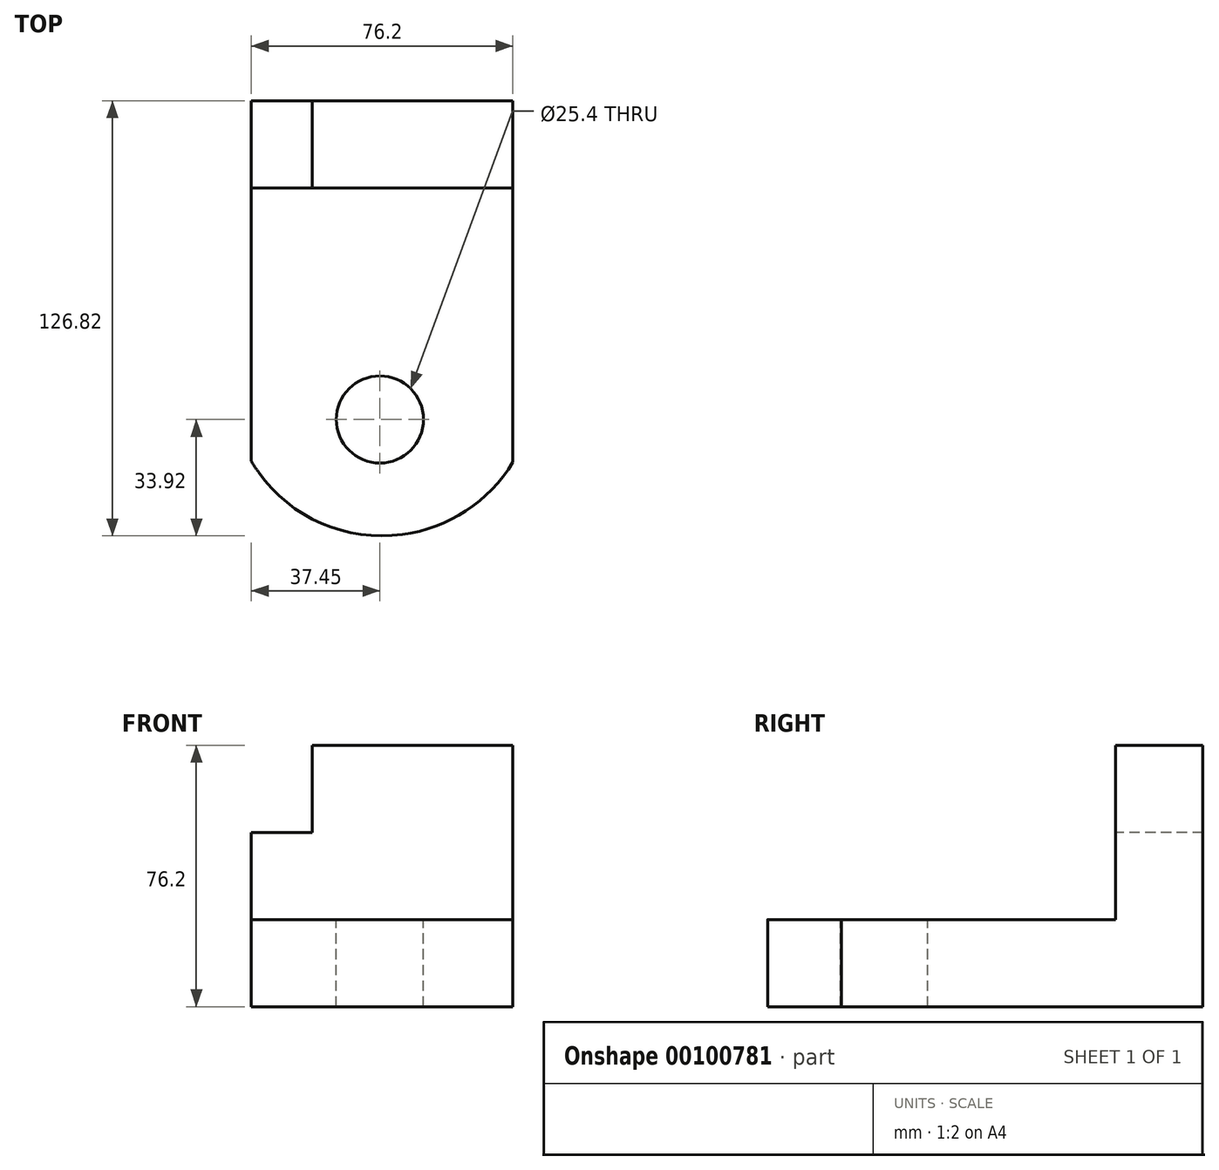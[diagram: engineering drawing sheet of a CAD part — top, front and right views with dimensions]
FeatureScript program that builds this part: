
annotation { "Feature Type Name" : "Feature", "Feature Type Description" : "" }
export const myFeature = defineFeature(function(context is Context, id is Id, definition is map)
    precondition{}
    {
        {
            var Q0;
            Q0=qCreatedBy(makeId("Top.planeOp"),FACE);
            var sketch = newSketch(context, id + "F0", { "sketchPlane" : qUnion([Q0])});
            skLineSegment(sketch, "E0.bottom", {"start": v(-37.45, 64) * mm, "end": v(38.75, 64) * mm});
            skLineSegment(sketch, "E0.top", {"start": v(-37.45, -63) * mm, "end": v(38.75, -63) * mm});
            skLineSegment(sketch, "E0.left", {"start": v(-37.45, 64) * mm, "end": v(-37.45, -63) * mm});
            skLineSegment(sketch, "E0.right", {"start": v(38.75, 64) * mm, "end": v(38.75, -63) * mm});
            skSolve(sketch);
        }
        {
            var Q0;
            Q0=makeQuery(id+"F0.imprint","IMPRINT",FACE,{"disambiguationData":[TD([[makeQuery(id+"F0.imprint","IMPRINT",EDGE,{"derivedFrom":sQuery(id+"F0.wireOp",EDGE,"E0.bottom")}),-1.0]])]});
            extrude(context, id + "F1", {"entities" : qUnion([Q0]), "depth" : 25.4 * mm});
        }
        {
            var Q0;
            Q0=makeQuery(id+"F1.opExtrude","CAP_FACE",FACE,{"disambiguationData":[OSD([sQuery(id+"F0.wireOp",EDGE,"E0.bottom"),sQuery(id+"F0.wireOp",EDGE,"E0.top"),sQuery(id+"F0.wireOp",EDGE,"E0.left"),sQuery(id+"F0.wireOp",EDGE,"E0.right")])],"isStart":false});
            var sketch = newSketch(context, id + "F2", { "sketchPlane" : qUnion([Q0])});
            skLineSegment(sketch, "E1.bottom", {"start": v(-37.45, 64) * mm, "end": v(38.75, 64) * mm});
            skLineSegment(sketch, "E1.top", {"start": v(-37.45, 38.6) * mm, "end": v(38.75, 38.6) * mm});
            skLineSegment(sketch, "E1.left", {"start": v(-37.45, 64) * mm, "end": v(-37.45, 38.6) * mm});
            skLineSegment(sketch, "E1.right", {"start": v(38.75, 64) * mm, "end": v(38.75, 38.6) * mm});
            skArc(sketch, "E2", {"start": v(-37.45, -47.3) * mm, "mid": v(0.6, -62.48) * mm, "end": v(38.75, -47.59) * mm});
            skSolve(sketch);
        }
        {
            var Q0;
            Q0=makeQuery(id+"F2.imprint","IMPRINT",FACE,{"disambiguationData":[TD([[makeQuery(id+"F2.imprint","IMPRINT",EDGE,{"derivedFrom":sQuery(id+"F2.wireOp",EDGE,"E1.bottom")}),-1.0]])]});
            extrude(context, id + "F3", {"entities" : qUnion([Q0]), "operationType" : NewBodyOperationType.ADD, "depth" : 25.4 * mm});
        }
        {
            var Q0;
            Q0=makeQuery(id+"F3.opExtrude","CAP_FACE",FACE,{"disambiguationData":[OSD([sQuery(id+"F2.wireOp",EDGE,"E1.bottom"),sQuery(id+"F2.wireOp",EDGE,"E1.top"),sQuery(id+"F2.wireOp",EDGE,"E1.left"),sQuery(id+"F2.wireOp",EDGE,"E1.right")])],"isStart":false});
            var sketch = newSketch(context, id + "F4", { "sketchPlane" : qUnion([Q0])});
            skLineSegment(sketch, "E3.bottom", {"start": v(-19.67, 64) * mm, "end": v(38.75, 64) * mm});
            skLineSegment(sketch, "E3.top", {"start": v(-19.67, 38.6) * mm, "end": v(38.75, 38.6) * mm});
            skLineSegment(sketch, "E3.left", {"start": v(-19.67, 64) * mm, "end": v(-19.67, 38.6) * mm});
            skLineSegment(sketch, "E3.right", {"start": v(38.75, 64) * mm, "end": v(38.75, 38.6) * mm});
            skSolve(sketch);
        }
        {
            var Q0;
            Q0=makeQuery(id+"F4.imprint","IMPRINT",FACE,{"disambiguationData":[TD([[makeQuery(id+"F4.imprint","IMPRINT",EDGE,{"derivedFrom":sQuery(id+"F4.wireOp",EDGE,"E3.bottom")}),-1.0]])]});
            extrude(context, id + "F5", {"entities" : qUnion([Q0]), "operationType" : NewBodyOperationType.ADD, "depth" : 25.4 * mm});
        }
        {
            var Q0;
            Q0=makeQuery(id+"F1.opExtrude","CAP_FACE",FACE,{"disambiguationData":[OSD([sQuery(id+"F0.wireOp",EDGE,"E0.bottom"),sQuery(id+"F0.wireOp",EDGE,"E0.top"),sQuery(id+"F0.wireOp",EDGE,"E0.left"),sQuery(id+"F0.wireOp",EDGE,"E0.right")])],"isStart":false});
            var sketch = newSketch(context, id + "F6", { "sketchPlane" : qUnion([Q0])});
            skArc(sketch, "E4", {"start": v(-37.45, -41.05) * mm, "mid": v(0.57, -62.77) * mm, "end": v(38.75, -41.34) * mm});
            skSolve(sketch);
        }
        {
            var Q0;
            Q0=makeQuery(id+"F6.imprint","IMPRINT",FACE,{"disambiguationData":[TD([[makeQuery(id+"F6.imprint","IMPRINT",EDGE,{"derivedFrom":makeQuery(id+"F1.opExtrude","CAP_EDGE",EDGE,{"disambiguationData":[OSD([sQuery(id+"F0.wireOp",EDGE,"E0.top")])],"isStart":false})}),1.0]])]});
            var sketch = newSketch(context, id + "F7", { "sketchPlane" : qUnion([Q0])});
            skCircle(sketch, "E5", {"center": v(0, -28.89) * mm, "radius": 12.7 * mm});
            skArc(sketch, "E6", {"start": v(-37.64, -40.63) * mm, "mid": v(0.49, -62.81) * mm, "end": v(38.57, -40.54) * mm});
            skSolve(sketch);
        }
        {
            var Q0;
            Q0 = qSketchRegion(id + "F7", true);
            extrude(context, id + "F8", {"entities" : qUnion([Q0]), "operationType" : NewBodyOperationType.REMOVE, "oppositeDirection" : true, "depth" : 25.4 * mm});
        }
        {
            var Q0;
            {var subQ0=sQuery(id+"F6.wireOp",EDGE,"E4");Q0=makeQuery(id+"F7.imprint","IMPRINT",FACE,{"disambiguationData":[TD([[makeQuery(id+"F7.imprint","IMPRINT",EDGE,{"derivedFrom":makeQuery(id+"F6.imprint","IMPRINT",EDGE,{"derivedFrom":subQ0})}),-1.0]])]});}
            extrude(context, id + "F9", {"entities" : qUnion([Q0]), "operationType" : NewBodyOperationType.REMOVE, "oppositeDirection" : true, "depth" : 25.4 * mm});
        }
        {
            var Q0;
            {var subQ0=makeQuery(id+"F1.opExtrude","CAP_EDGE",EDGE,{"disambiguationData":[OSD([sQuery(id+"F0.wireOp",EDGE,"E0.top")])],"isStart":false});Q0=makeQuery(id+"F7.imprint","IMPRINT",FACE,{"disambiguationData":[TD([[makeQuery(id+"F7.imprint","IMPRINT",EDGE,{"derivedFrom":makeQuery(id+"F6.imprint","IMPRINT",EDGE,{"derivedFrom":subQ0})}),1.0]])]});}
            extrude(context, id + "F10", {"entities" : qUnion([Q0]), "operationType" : NewBodyOperationType.REMOVE, "endBound" : BoundingType.THROUGH_ALL, "oppositeDirection" : true, "depth" : 25.4 * mm});
        }
    });
